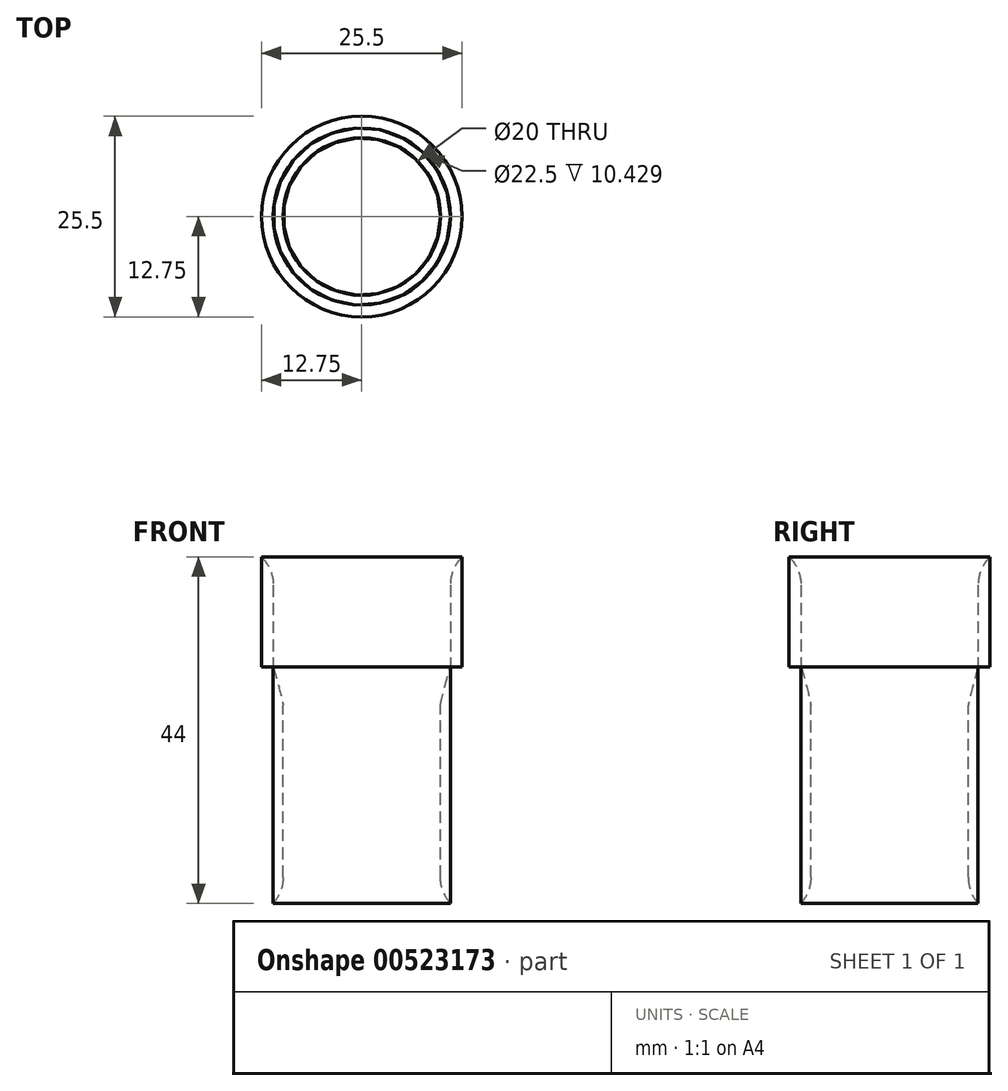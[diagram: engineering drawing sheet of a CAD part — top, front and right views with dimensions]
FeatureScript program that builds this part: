
annotation { "Feature Type Name" : "Feature", "Feature Type Description" : "" }
export const myFeature = defineFeature(function(context is Context, id is Id, definition is map)
    precondition{}
    {
        {
            var Q0;
            Q0=qCreatedBy(makeId("Top.planeOp"),FACE);
            var sketch = newSketch(context, id + "F0", { "sketchPlane" : qUnion([Q0])});
            skCircle(sketch, "E0", {"center": v(0, 0) * mm, "radius": 12.75 * mm});
            skCircle(sketch, "E1", {"center": v(0, 0) * mm, "radius": 11.25 * mm});
            skSolve(sketch);
        }
        {
            var Q0;
            Q0 = qSketchRegion(id + "F0", true);
            extrude(context, id + "F1", {"entities" : qUnion([Q0]), "depth" : 14 * mm, "offsetDistance" : 25 * mm});
        }
        {
            var Q0;
            Q0=qCreatedBy(makeId("Top.planeOp"),FACE);
            var sketch = newSketch(context, id + "F2", { "sketchPlane" : qUnion([Q0])});
            skCircle(sketch, "E2", {"center": v(0, 0) * mm, "radius": 11.25 * mm});
            skCircle(sketch, "E3", {"center": v(0, 0) * mm, "radius": 10 * mm});
            skSolve(sketch);
        }
        {
            var Q0;
            Q0 = qSketchRegion(id + "F2", true);
            extrude(context, id + "F3", {"entities" : qUnion([Q0]), "operationType" : NewBodyOperationType.ADD, "oppositeDirection" : true, "depth" : 30 * mm, "offsetDistance" : 25 * mm});
        }
        {
            var Q0;
            Q0=makeQuery(id+"F3.opExtrude","CAP_EDGE",EDGE,{"disambiguationData":[OSD([sQuery(id+"F2.wireOp",EDGE,"E3")])],"isStart":true});
            fillet(context, id + "F4", {"entities" : qUnion([Q0]), "radius" : 10 * mm, "tangentPropagation" : true, "rho" : .1, "crossSection" : FilletCrossSection.CONIC, "allowEdgeOverflow" : false});
        }
        {
            var Q0;
            Q0=makeQuery(id+"F1.opExtrude","CAP_EDGE",EDGE,{"disambiguationData":[OSD([sQuery(id+"F0.wireOp",EDGE,"E1")])],"isStart":false});
            fillet(context, id + "F5", {"entities" : qUnion([Q0]), "radius" : 5 * mm, "tangentPropagation" : true, "allowEdgeOverflow" : false});
        }
        {
            var Q0;
            Q0=makeQuery(id+"F3.opExtrude","CAP_EDGE",EDGE,{"disambiguationData":[OSD([sQuery(id+"F2.wireOp",EDGE,"E3")])],"isStart":false});
            fillet(context, id + "F6", {"entities" : qUnion([Q0]), "radius" : 5 * mm, "tangentPropagation" : true, "allowEdgeOverflow" : false});
        }
    });
